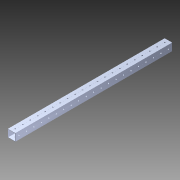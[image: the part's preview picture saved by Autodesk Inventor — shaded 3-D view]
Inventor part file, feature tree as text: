
AUTODESK INVENTOR PART (.ipt)
format: ipt  version: 2014 SP1 (Build 180222100, 222)  size: 1,595,392 bytes
history: native  units: in
note: dims shown in document units (in); Inventor stores cm internally (conversion verified against a paired STEP export)
features: extrude x4, sketch x4, pattern_circular x1, other x1, mirror x1, imported_body x1
ambient origin geometry x8: Origin, YZ Plane, XZ Plane, XY Plane, X Axis, Y Axis, Z Axis, Center Point
bodies: Body1 (feature_tree)
feature tree (12):
  pattern_circular  "CirPattern2"
  other  "1x1 tube1"
  extrude  "Extrusion1"  Depth=16.0in TaperAngle=0.0deg
  mirror  "Mirror1"
  extrude  "Extrusion2"  Depth=1.0in TaperAngle=0.0deg
  extrude  "Extrusion3"  [1 undecoded]
  extrude  "Extrusion4"  [1 undecoded]
  imported_body  "Base1"
  sketch  "Sketch1"  dims[d0=38.0in d1=0.0in d2=16.0in d3=0.0in]
  sketch  "Sketch3"  dims[d4=1.0in d5=0.0in d6=4.0in d7=0.0in]
  sketch  "Sketch4"
  sketch  "Sketch5"
note: 2 required parameter values undecoded (feature->parameter linkage not recoverable at this tier; creation-order binding heuristic only, values carry confidence <= 0.55)
